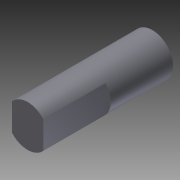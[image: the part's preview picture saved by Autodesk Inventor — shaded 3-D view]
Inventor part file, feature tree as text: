
AUTODESK INVENTOR PART (.ipt)
format: ipt  version: 2012 (Build 160160000, 160)  size: 79,360 bytes
history: native  units: in
note: dims shown in document units (in); Inventor stores cm internally (conversion verified against a paired STEP export)
features: other x3, sketch x2
ambient origin geometry x8: Origin, YZ Plane, XZ Plane, XY Plane, X Axis, Y Axis, Z Axis, Center Point
bodies: Solid1 (feature_tree)
feature tree (5):
  other  "shaft.ipt"
  other  "Solid1::shaft.ipt"
  sketch  "Sketch1"  dims[d0=0.3937in]
  sketch  "Sketch2"
  other  "TaggingFeature1"
